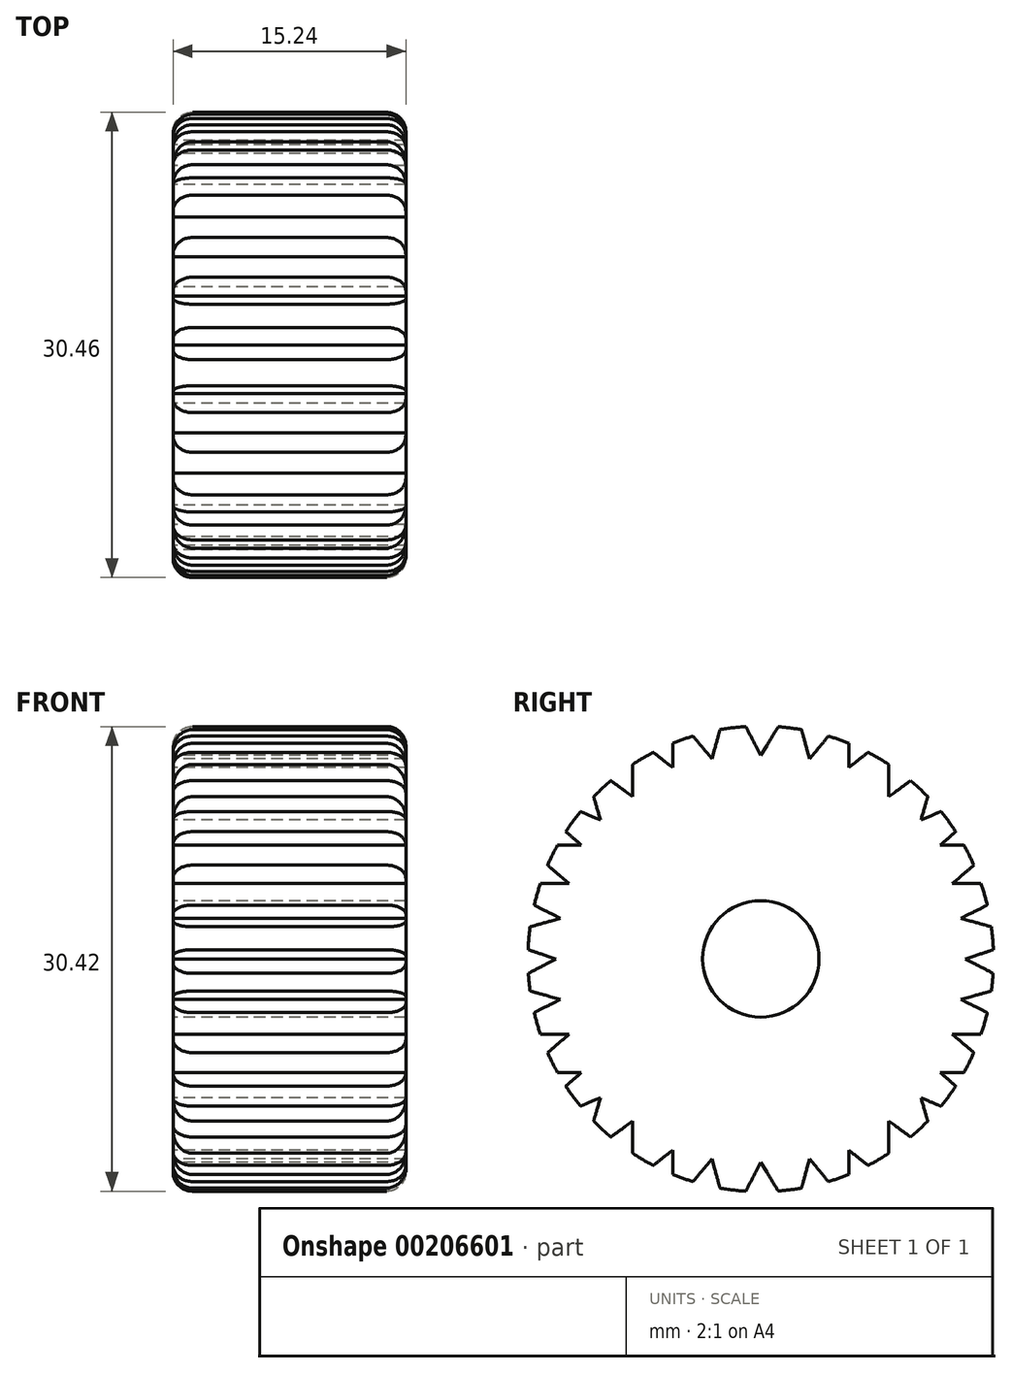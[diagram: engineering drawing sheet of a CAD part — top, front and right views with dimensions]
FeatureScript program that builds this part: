
annotation { "Feature Type Name" : "Feature", "Feature Type Description" : "" }
export const myFeature = defineFeature(function(context is Context, id is Id, definition is map)
    precondition{}
    {
        {
            var Q0;
            Q0=qCreatedBy(makeId("Right.planeOp"),FACE);
            var sketch = newSketch(context, id + "F0", { "sketchPlane" : qUnion([Q0])});
            skCircle(sketch, "E0", {"center": v(0, 0) * mm, "radius": 15.24 * mm});
            skLineSegment(sketch, "E1", {"start": v(11.8, 9.65) * mm, "end": v(10.5, 9.1) * mm});
            skLineSegment(sketch, "E2", {"start": v(10.5, 9.1) * mm, "end": v(10.94, 10.61) * mm});
            skLineSegment(sketch, "E3", {"start": v(12.76, 8.33) * mm, "end": v(11.74, 7.44) * mm});
            skLineSegment(sketch, "E4", {"start": v(11.74, 7.44) * mm, "end": v(13.3, 7.44) * mm});
            skLineSegment(sketch, "E5", {"start": v(14.83, 3.52) * mm, "end": v(13.11, 2.65) * mm});
            skLineSegment(sketch, "E6", {"start": v(13.11, 2.65) * mm, "end": v(15.1, 2.1) * mm});
            skLineSegment(sketch, "E7", {"start": v(13.95, 6.14) * mm, "end": v(12.54, 4.93) * mm});
            skLineSegment(sketch, "E8", {"start": v(12.54, 4.93) * mm, "end": v(14.42, 4.93) * mm});
            skLineSegment(sketch, "E9", {"start": v(15.23, 0.6) * mm, "end": v(13.4, 0) * mm});
            skLineSegment(sketch, "E10", {"start": v(13.4, 0) * mm, "end": v(15.21, -0.95) * mm});
            skLineSegment(sketch, "E11", {"start": v(9.8, 11.67) * mm, "end": v(8.38, 10.61) * mm});
            skLineSegment(sketch, "E12", {"start": v(8.38, 10.61) * mm, "end": v(8.38, 12.73) * mm});
            skLineSegment(sketch, "E13", {"start": v(7.03, 13.52) * mm, "end": v(5.76, 12.51) * mm});
            skLineSegment(sketch, "E14", {"start": v(5.76, 12.51) * mm, "end": v(5.76, 14.11) * mm});
            skLineSegment(sketch, "E15", {"start": v(4.43, 14.58) * mm, "end": v(3.2, 13.08) * mm});
            skLineSegment(sketch, "E16", {"start": v(3.2, 13.08) * mm, "end": v(2.67, 15) * mm});
            skLineSegment(sketch, "E17", {"start": v(1.15, 15.2) * mm, "end": v(0, 13.31) * mm});
            skPoint(sketch, "E17.endSnap0", {"position": v(5.76, 13.31) * mm});
            skLineSegment(sketch, "E18", {"start": v(0, 13.31) * mm, "end": v(-0.97, 15.2) * mm});
            skLineSegment(sketch, "E19.MirrorCS", {"start": v(-13.11, 2.65) * mm, "end": v(-15.1, 2.1) * mm});
            skLineSegment(sketch, "E20.MirrorCS", {"start": v(-14.83, 3.52) * mm, "end": v(-13.11, 2.65) * mm});
            skLineSegment(sketch, "E21.MirrorCS", {"start": v(-15.23, 0.6) * mm, "end": v(-13.4, 0) * mm});
            skLineSegment(sketch, "E22.MirrorCS", {"start": v(-13.4, 0) * mm, "end": v(-15.21, -0.95) * mm});
            skLineSegment(sketch, "E23.MirrorCS", {"start": v(-12.54, 4.93) * mm, "end": v(-14.42, 4.93) * mm});
            skLineSegment(sketch, "E24.MirrorCS", {"start": v(-13.95, 6.14) * mm, "end": v(-12.54, 4.93) * mm});
            skLineSegment(sketch, "E25.MirrorCS", {"start": v(-11.74, 7.44) * mm, "end": v(-13.3, 7.44) * mm});
            skLineSegment(sketch, "E26.MirrorCS", {"start": v(-12.76, 8.33) * mm, "end": v(-11.74, 7.44) * mm});
            skLineSegment(sketch, "E27.MirrorCS", {"start": v(-11.8, 9.65) * mm, "end": v(-10.5, 9.1) * mm});
            skLineSegment(sketch, "E28.MirrorCS", {"start": v(-10.5, 9.1) * mm, "end": v(-10.94, 10.61) * mm});
            skLineSegment(sketch, "E29.MirrorCS", {"start": v(-9.8, 11.67) * mm, "end": v(-8.38, 10.61) * mm});
            skLineSegment(sketch, "E30.MirrorCS", {"start": v(-8.38, 10.61) * mm, "end": v(-8.38, 12.73) * mm});
            skPoint(sketch, "E31.MirrorP", {"position": v(-5.76, 13.31) * mm});
            skLineSegment(sketch, "E32.MirrorCS", {"start": v(-7.03, 13.52) * mm, "end": v(-5.76, 12.51) * mm});
            skLineSegment(sketch, "E33.MirrorCS", {"start": v(-5.76, 12.51) * mm, "end": v(-5.76, 14.11) * mm});
            skLineSegment(sketch, "E34.MirrorCS", {"start": v(-4.43, 14.58) * mm, "end": v(-3.2, 13.08) * mm});
            skLineSegment(sketch, "E35.MirrorCS", {"start": v(-3.2, 13.08) * mm, "end": v(-2.67, 15) * mm});
            skLineSegment(sketch, "E36.MirrorCS", {"start": v(13.11, -2.65) * mm, "end": v(15.1, -2.1) * mm});
            skLineSegment(sketch, "E37.MirrorCS", {"start": v(14.83, -3.52) * mm, "end": v(13.11, -2.65) * mm});
            skLineSegment(sketch, "E38.MirrorCS", {"start": v(12.54, -4.93) * mm, "end": v(14.42, -4.93) * mm});
            skLineSegment(sketch, "E39.MirrorCS", {"start": v(13.95, -6.14) * mm, "end": v(12.54, -4.93) * mm});
            skLineSegment(sketch, "E40.MirrorCS", {"start": v(11.74, -7.44) * mm, "end": v(13.3, -7.44) * mm});
            skLineSegment(sketch, "E41.MirrorCS", {"start": v(12.76, -8.33) * mm, "end": v(11.74, -7.44) * mm});
            skLineSegment(sketch, "E42.MirrorCS", {"start": v(11.8, -9.65) * mm, "end": v(10.5, -9.1) * mm});
            skLineSegment(sketch, "E43.MirrorCS", {"start": v(10.5, -9.1) * mm, "end": v(10.94, -10.61) * mm});
            skLineSegment(sketch, "E44.MirrorCS", {"start": v(9.8, -11.67) * mm, "end": v(8.38, -10.61) * mm});
            skLineSegment(sketch, "E45.MirrorCS", {"start": v(8.38, -10.61) * mm, "end": v(8.38, -12.73) * mm});
            skLineSegment(sketch, "E46.MirrorCS", {"start": v(7.03, -13.52) * mm, "end": v(5.76, -12.51) * mm});
            skLineSegment(sketch, "E47.MirrorCS", {"start": v(5.76, -12.51) * mm, "end": v(5.76, -14.11) * mm});
            skLineSegment(sketch, "E48.MirrorCS", {"start": v(4.43, -14.58) * mm, "end": v(3.2, -13.08) * mm});
            skLineSegment(sketch, "E49.MirrorCS", {"start": v(3.2, -13.08) * mm, "end": v(2.67, -15) * mm});
            skLineSegment(sketch, "E50.MirrorCS", {"start": v(1.15, -15.2) * mm, "end": v(0, -13.31) * mm});
            skLineSegment(sketch, "E51.MirrorCS", {"start": v(0, -13.31) * mm, "end": v(-0.97, -15.2) * mm});
            skLineSegment(sketch, "E52.MirrorCS", {"start": v(-3.2, -13.08) * mm, "end": v(-2.67, -15) * mm});
            skLineSegment(sketch, "E53.MirrorCS", {"start": v(-4.43, -14.58) * mm, "end": v(-3.2, -13.08) * mm});
            skLineSegment(sketch, "E54.MirrorCS", {"start": v(-7.03, -13.52) * mm, "end": v(-5.76, -12.51) * mm});
            skLineSegment(sketch, "E55.MirrorCS", {"start": v(-5.76, -12.51) * mm, "end": v(-5.76, -14.11) * mm});
            skLineSegment(sketch, "E56.MirrorCS", {"start": v(-8.38, -10.61) * mm, "end": v(-8.38, -12.73) * mm});
            skLineSegment(sketch, "E57.MirrorCS", {"start": v(-9.8, -11.67) * mm, "end": v(-8.38, -10.61) * mm});
            skLineSegment(sketch, "E58.MirrorCS", {"start": v(-10.5, -9.1) * mm, "end": v(-10.94, -10.61) * mm});
            skLineSegment(sketch, "E59.MirrorCS", {"start": v(-11.8, -9.65) * mm, "end": v(-10.5, -9.1) * mm});
            skLineSegment(sketch, "E60.MirrorCS", {"start": v(-12.76, -8.33) * mm, "end": v(-11.74, -7.44) * mm});
            skLineSegment(sketch, "E61.MirrorCS", {"start": v(-11.74, -7.44) * mm, "end": v(-13.3, -7.44) * mm});
            skLineSegment(sketch, "E62.MirrorCS", {"start": v(-13.95, -6.14) * mm, "end": v(-12.54, -4.93) * mm});
            skLineSegment(sketch, "E63.MirrorCS", {"start": v(-12.54, -4.93) * mm, "end": v(-14.42, -4.93) * mm});
            skLineSegment(sketch, "E64.MirrorCS", {"start": v(-14.83, -3.52) * mm, "end": v(-13.11, -2.65) * mm});
            skLineSegment(sketch, "E65.MirrorCS", {"start": v(-13.11, -2.65) * mm, "end": v(-15.1, -2.1) * mm});
            skSolve(sketch);
        }
        {
            var Q0;
            {var subQ14=sQuery(id+"F0.wireOp",EDGE,"E1");Q0=makeQuery(id+"F0.imprint","IMPRINT",FACE,{"disambiguationData":[TD([[makeQuery(id+"F0.imprint","IMPRINT",EDGE,{"derivedFrom":subQ14}),1.0]])]});}
            extrude(context, id + "F1", {"entities" : qUnion([Q0]), "depth" : 15.24 * mm});
        }
        {
            var Q0;
            Q0=makeQuery(id+"F1.opExtrude","CAP_FACE",FACE,{"disambiguationData":[OSD([sQuery(id+"F0.wireOp",EDGE,"E0"),sQuery(id+"F0.wireOp",EDGE,"E1"),sQuery(id+"F0.wireOp",EDGE,"E2"),sQuery(id+"F0.wireOp",EDGE,"E3"),sQuery(id+"F0.wireOp",EDGE,"E4"),sQuery(id+"F0.wireOp",EDGE,"E5"),sQuery(id+"F0.wireOp",EDGE,"E6"),sQuery(id+"F0.wireOp",EDGE,"E7"),sQuery(id+"F0.wireOp",EDGE,"E8"),sQuery(id+"F0.wireOp",EDGE,"E9"),sQuery(id+"F0.wireOp",EDGE,"E10"),sQuery(id+"F0.wireOp",EDGE,"E11"),sQuery(id+"F0.wireOp",EDGE,"E12"),sQuery(id+"F0.wireOp",EDGE,"E13"),sQuery(id+"F0.wireOp",EDGE,"E14"),sQuery(id+"F0.wireOp",EDGE,"E15"),sQuery(id+"F0.wireOp",EDGE,"E16"),sQuery(id+"F0.wireOp",EDGE,"E17"),sQuery(id+"F0.wireOp",EDGE,"E18"),sQuery(id+"F0.wireOp",EDGE,"E19.MirrorCS"),sQuery(id+"F0.wireOp",EDGE,"E20.MirrorCS"),sQuery(id+"F0.wireOp",EDGE,"E21.MirrorCS"),sQuery(id+"F0.wireOp",EDGE,"E22.MirrorCS"),sQuery(id+"F0.wireOp",EDGE,"E23.MirrorCS"),sQuery(id+"F0.wireOp",EDGE,"E24.MirrorCS"),sQuery(id+"F0.wireOp",EDGE,"E25.MirrorCS"),sQuery(id+"F0.wireOp",EDGE,"E26.MirrorCS"),sQuery(id+"F0.wireOp",EDGE,"E27.MirrorCS"),sQuery(id+"F0.wireOp",EDGE,"E28.MirrorCS"),sQuery(id+"F0.wireOp",EDGE,"E29.MirrorCS"),sQuery(id+"F0.wireOp",EDGE,"E30.MirrorCS"),sQuery(id+"F0.wireOp",EDGE,"E32.MirrorCS"),sQuery(id+"F0.wireOp",EDGE,"E33.MirrorCS"),sQuery(id+"F0.wireOp",EDGE,"E34.MirrorCS"),sQuery(id+"F0.wireOp",EDGE,"E35.MirrorCS"),sQuery(id+"F0.wireOp",EDGE,"E36.MirrorCS"),sQuery(id+"F0.wireOp",EDGE,"E37.MirrorCS"),sQuery(id+"F0.wireOp",EDGE,"E38.MirrorCS"),sQuery(id+"F0.wireOp",EDGE,"E39.MirrorCS"),sQuery(id+"F0.wireOp",EDGE,"E40.MirrorCS"),sQuery(id+"F0.wireOp",EDGE,"E41.MirrorCS"),sQuery(id+"F0.wireOp",EDGE,"E42.MirrorCS"),sQuery(id+"F0.wireOp",EDGE,"E43.MirrorCS"),sQuery(id+"F0.wireOp",EDGE,"E44.MirrorCS"),sQuery(id+"F0.wireOp",EDGE,"E45.MirrorCS"),sQuery(id+"F0.wireOp",EDGE,"E46.MirrorCS"),sQuery(id+"F0.wireOp",EDGE,"E47.MirrorCS"),sQuery(id+"F0.wireOp",EDGE,"E48.MirrorCS"),sQuery(id+"F0.wireOp",EDGE,"E49.MirrorCS"),sQuery(id+"F0.wireOp",EDGE,"E50.MirrorCS"),sQuery(id+"F0.wireOp",EDGE,"E51.MirrorCS"),sQuery(id+"F0.wireOp",EDGE,"E52.MirrorCS"),sQuery(id+"F0.wireOp",EDGE,"E53.MirrorCS"),sQuery(id+"F0.wireOp",EDGE,"E54.MirrorCS"),sQuery(id+"F0.wireOp",EDGE,"E55.MirrorCS"),sQuery(id+"F0.wireOp",EDGE,"E56.MirrorCS"),sQuery(id+"F0.wireOp",EDGE,"E57.MirrorCS"),sQuery(id+"F0.wireOp",EDGE,"E58.MirrorCS"),sQuery(id+"F0.wireOp",EDGE,"E59.MirrorCS"),sQuery(id+"F0.wireOp",EDGE,"E60.MirrorCS"),sQuery(id+"F0.wireOp",EDGE,"E61.MirrorCS"),sQuery(id+"F0.wireOp",EDGE,"E62.MirrorCS"),sQuery(id+"F0.wireOp",EDGE,"E63.MirrorCS"),sQuery(id+"F0.wireOp",EDGE,"E64.MirrorCS"),sQuery(id+"F0.wireOp",EDGE,"E65.MirrorCS")])],"isStart":true});
            var sketch = newSketch(context, id + "F2", { "sketchPlane" : qUnion([Q0])});
            skCircle(sketch, "E66", {"center": v(0, 0) * mm, "radius": 3.81 * mm});
            skSolve(sketch);
        }
        {
            var Q0;
            Q0=makeQuery(id+"F2.imprint","IMPRINT",FACE,{"disambiguationData":[TD([[makeQuery(id+"F2.imprint","IMPRINT",EDGE,{"derivedFrom":sQuery(id+"F2.wireOp",EDGE,"E66")}),1.0]])]});
            var Q1;
            Q1=sQuery(id+"F2.wireOp",EDGE,"E66");
            extrude(context, id + "F3", {"entities" : qUnion([Q0]), "operationType" : NewBodyOperationType.REMOVE, "surfaceEntities" : qUnion([Q1]), "oppositeDirection" : true, "depth" : 38.1 * mm});
        }
        {
            var Q0;
            {var subQ0=sQuery(id+"F0.wireOp",EDGE,"E0");Q0=makeQuery(id+"F1.opExtrude","CAP_EDGE",EDGE,{"disambiguationData":[OSD([subQ0]),TDD([makeQuery(id+"F0.imprint","IMPRINT",EDGE,{"disambiguationData":[TD([[makeQuery(id+"F0.imprint","INTERSECT",VERTEX,{"derivedFrom":[subQ0,sQuery(id+"F0.wireOp",EDGE,"E51.MirrorCS")]}),1.0]])],"derivedFrom":subQ0})])],"isStart":true});}
            var Q1;
            {var subQ0=sQuery(id+"F0.wireOp",EDGE,"E0");Q1=makeQuery(id+"F1.opExtrude","CAP_EDGE",EDGE,{"disambiguationData":[OSD([subQ0]),TDD([makeQuery(id+"F0.imprint","IMPRINT",EDGE,{"disambiguationData":[TD([[makeQuery(id+"F0.imprint","INTERSECT",VERTEX,{"derivedFrom":[subQ0,sQuery(id+"F0.wireOp",EDGE,"E49.MirrorCS")]}),1.0]])],"derivedFrom":subQ0})])],"isStart":true});}
            var Q2;
            {var subQ0=sQuery(id+"F0.wireOp",EDGE,"E0");Q2=makeQuery(id+"F1.opExtrude","CAP_EDGE",EDGE,{"disambiguationData":[OSD([subQ0]),TDD([makeQuery(id+"F0.imprint","IMPRINT",EDGE,{"disambiguationData":[TD([[makeQuery(id+"F0.imprint","INTERSECT",VERTEX,{"derivedFrom":[subQ0,sQuery(id+"F0.wireOp",EDGE,"E47.MirrorCS")]}),1.0]])],"derivedFrom":subQ0})])],"isStart":true});}
            var Q3;
            {var subQ0=sQuery(id+"F0.wireOp",EDGE,"E0");Q3=makeQuery(id+"F1.opExtrude","CAP_EDGE",EDGE,{"disambiguationData":[OSD([subQ0]),TDD([makeQuery(id+"F0.imprint","IMPRINT",EDGE,{"disambiguationData":[TD([[makeQuery(id+"F0.imprint","INTERSECT",VERTEX,{"derivedFrom":[subQ0,sQuery(id+"F0.wireOp",EDGE,"E61.MirrorCS")]}),1.0]])],"derivedFrom":subQ0})])],"isStart":true});}
            var Q4;
            {var subQ0=sQuery(id+"F0.wireOp",EDGE,"E0");Q4=makeQuery(id+"F1.opExtrude","CAP_EDGE",EDGE,{"disambiguationData":[OSD([subQ0]),TDD([makeQuery(id+"F0.imprint","IMPRINT",EDGE,{"disambiguationData":[TD([[makeQuery(id+"F0.imprint","INTERSECT",VERTEX,{"derivedFrom":[subQ0,sQuery(id+"F0.wireOp",EDGE,"E59.MirrorCS")]}),1.0]])],"derivedFrom":subQ0})])],"isStart":true});}
            var Q5;
            {var subQ0=sQuery(id+"F0.wireOp",EDGE,"E0");Q5=makeQuery(id+"F1.opExtrude","CAP_EDGE",EDGE,{"disambiguationData":[OSD([subQ0]),TDD([makeQuery(id+"F0.imprint","IMPRINT",EDGE,{"disambiguationData":[TD([[makeQuery(id+"F0.imprint","INTERSECT",VERTEX,{"derivedFrom":[subQ0,sQuery(id+"F0.wireOp",EDGE,"E57.MirrorCS")]}),1.0]])],"derivedFrom":subQ0})])],"isStart":true});}
            var Q6;
            {var subQ0=sQuery(id+"F0.wireOp",EDGE,"E0");Q6=makeQuery(id+"F1.opExtrude","CAP_EDGE",EDGE,{"disambiguationData":[OSD([subQ0]),TDD([makeQuery(id+"F0.imprint","IMPRINT",EDGE,{"disambiguationData":[TD([[makeQuery(id+"F0.imprint","INTERSECT",VERTEX,{"derivedFrom":[subQ0,sQuery(id+"F0.wireOp",EDGE,"E54.MirrorCS")]}),1.0]])],"derivedFrom":subQ0})])],"isStart":true});}
            var Q7;
            {var subQ0=sQuery(id+"F0.wireOp",EDGE,"E0");Q7=makeQuery(id+"F1.opExtrude","CAP_EDGE",EDGE,{"disambiguationData":[OSD([subQ0]),TDD([makeQuery(id+"F0.imprint","IMPRINT",EDGE,{"disambiguationData":[TD([[makeQuery(id+"F0.imprint","INTERSECT",VERTEX,{"derivedFrom":[subQ0,sQuery(id+"F0.wireOp",EDGE,"E63.MirrorCS")]}),1.0]])],"derivedFrom":subQ0})])],"isStart":true});}
            var Q8;
            {var subQ0=sQuery(id+"F0.wireOp",EDGE,"E0");Q8=makeQuery(id+"F1.opExtrude","CAP_EDGE",EDGE,{"disambiguationData":[OSD([subQ0]),TDD([makeQuery(id+"F0.imprint","IMPRINT",EDGE,{"disambiguationData":[TD([[makeQuery(id+"F0.imprint","INTERSECT",VERTEX,{"derivedFrom":[subQ0,sQuery(id+"F0.wireOp",EDGE,"E19.MirrorCS")]}),-1.0]])],"derivedFrom":subQ0})])],"isStart":true});}
            var Q9;
            {var subQ0=sQuery(id+"F0.wireOp",EDGE,"E0");Q9=makeQuery(id+"F1.opExtrude","CAP_EDGE",EDGE,{"disambiguationData":[OSD([subQ0]),TDD([makeQuery(id+"F0.imprint","IMPRINT",EDGE,{"disambiguationData":[TD([[makeQuery(id+"F0.imprint","INTERSECT",VERTEX,{"derivedFrom":[subQ0,sQuery(id+"F0.wireOp",EDGE,"E22.MirrorCS")]}),-1.0]])],"derivedFrom":subQ0})])],"isStart":true});}
            var Q10;
            {var subQ0=sQuery(id+"F0.wireOp",EDGE,"E0");Q10=makeQuery(id+"F1.opExtrude","CAP_EDGE",EDGE,{"disambiguationData":[OSD([subQ0]),TDD([makeQuery(id+"F0.imprint","IMPRINT",EDGE,{"disambiguationData":[TD([[makeQuery(id+"F0.imprint","INTERSECT",VERTEX,{"derivedFrom":[subQ0,sQuery(id+"F0.wireOp",EDGE,"E20.MirrorCS")]}),1.0]])],"derivedFrom":subQ0})])],"isStart":true});}
            var Q11;
            {var subQ0=sQuery(id+"F0.wireOp",EDGE,"E0");Q11=makeQuery(id+"F1.opExtrude","CAP_EDGE",EDGE,{"disambiguationData":[OSD([subQ0]),TDD([makeQuery(id+"F0.imprint","IMPRINT",EDGE,{"disambiguationData":[TD([[makeQuery(id+"F0.imprint","INTERSECT",VERTEX,{"derivedFrom":[subQ0,sQuery(id+"F0.wireOp",EDGE,"E24.MirrorCS")]}),1.0]])],"derivedFrom":subQ0})])],"isStart":true});}
            var Q12;
            {var subQ0=sQuery(id+"F0.wireOp",EDGE,"E0");Q12=makeQuery(id+"F1.opExtrude","CAP_EDGE",EDGE,{"disambiguationData":[OSD([subQ0]),TDD([makeQuery(id+"F0.imprint","IMPRINT",EDGE,{"disambiguationData":[TD([[makeQuery(id+"F0.imprint","INTERSECT",VERTEX,{"derivedFrom":[subQ0,sQuery(id+"F0.wireOp",EDGE,"E26.MirrorCS")]}),1.0]])],"derivedFrom":subQ0})])],"isStart":true});}
            var Q13;
            {var subQ0=sQuery(id+"F0.wireOp",EDGE,"E0");Q13=makeQuery(id+"F1.opExtrude","CAP_EDGE",EDGE,{"disambiguationData":[OSD([subQ0]),TDD([makeQuery(id+"F0.imprint","IMPRINT",EDGE,{"disambiguationData":[TD([[makeQuery(id+"F0.imprint","INTERSECT",VERTEX,{"derivedFrom":[subQ0,sQuery(id+"F0.wireOp",EDGE,"E53.MirrorCS")]}),1.0]])],"derivedFrom":subQ0})])],"isStart":true});}
            var Q14;
            {var subQ0=sQuery(id+"F0.wireOp",EDGE,"E0");Q14=makeQuery(id+"F1.opExtrude","CAP_EDGE",EDGE,{"disambiguationData":[OSD([subQ0]),TDD([makeQuery(id+"F0.imprint","IMPRINT",EDGE,{"disambiguationData":[TD([[makeQuery(id+"F0.imprint","INTERSECT",VERTEX,{"derivedFrom":[subQ0,sQuery(id+"F0.wireOp",EDGE,"E45.MirrorCS")]}),1.0]])],"derivedFrom":subQ0})])],"isStart":true});}
            var Q15;
            {var subQ0=sQuery(id+"F0.wireOp",EDGE,"E0");Q15=makeQuery(id+"F1.opExtrude","CAP_EDGE",EDGE,{"disambiguationData":[OSD([subQ0]),TDD([makeQuery(id+"F0.imprint","IMPRINT",EDGE,{"disambiguationData":[TD([[makeQuery(id+"F0.imprint","INTERSECT",VERTEX,{"derivedFrom":[subQ0,sQuery(id+"F0.wireOp",EDGE,"E43.MirrorCS")]}),1.0]])],"derivedFrom":subQ0})])],"isStart":true});}
            var Q16;
            {var subQ0=sQuery(id+"F0.wireOp",EDGE,"E0");Q16=makeQuery(id+"F1.opExtrude","CAP_EDGE",EDGE,{"disambiguationData":[OSD([subQ0]),TDD([makeQuery(id+"F0.imprint","IMPRINT",EDGE,{"disambiguationData":[TD([[makeQuery(id+"F0.imprint","INTERSECT",VERTEX,{"derivedFrom":[subQ0,sQuery(id+"F0.wireOp",EDGE,"E41.MirrorCS")]}),1.0]])],"derivedFrom":subQ0})])],"isStart":true});}
            var Q17;
            {var subQ0=sQuery(id+"F0.wireOp",EDGE,"E0");Q17=makeQuery(id+"F1.opExtrude","CAP_EDGE",EDGE,{"disambiguationData":[OSD([subQ0]),TDD([makeQuery(id+"F0.imprint","IMPRINT",EDGE,{"disambiguationData":[TD([[makeQuery(id+"F0.imprint","INTERSECT",VERTEX,{"derivedFrom":[subQ0,sQuery(id+"F0.wireOp",EDGE,"E39.MirrorCS")]}),1.0]])],"derivedFrom":subQ0})])],"isStart":true});}
            var Q18;
            {var subQ0=sQuery(id+"F0.wireOp",EDGE,"E0");Q18=makeQuery(id+"F1.opExtrude","CAP_EDGE",EDGE,{"disambiguationData":[OSD([subQ0]),TDD([makeQuery(id+"F0.imprint","IMPRINT",EDGE,{"disambiguationData":[TD([[makeQuery(id+"F0.imprint","INTERSECT",VERTEX,{"derivedFrom":[subQ0,sQuery(id+"F0.wireOp",EDGE,"E28.MirrorCS")]}),1.0]])],"derivedFrom":subQ0})])],"isStart":true});}
            var Q19;
            {var subQ0=sQuery(id+"F0.wireOp",EDGE,"E0");Q19=makeQuery(id+"F1.opExtrude","CAP_EDGE",EDGE,{"disambiguationData":[OSD([subQ0]),TDD([makeQuery(id+"F0.imprint","IMPRINT",EDGE,{"disambiguationData":[TD([[makeQuery(id+"F0.imprint","INTERSECT",VERTEX,{"derivedFrom":[subQ0,sQuery(id+"F0.wireOp",EDGE,"E30.MirrorCS")]}),1.0]])],"derivedFrom":subQ0})])],"isStart":true});}
            var Q20;
            {var subQ0=sQuery(id+"F0.wireOp",EDGE,"E0");Q20=makeQuery(id+"F1.opExtrude","CAP_EDGE",EDGE,{"disambiguationData":[OSD([subQ0]),TDD([makeQuery(id+"F0.imprint","IMPRINT",EDGE,{"disambiguationData":[TD([[makeQuery(id+"F0.imprint","INTERSECT",VERTEX,{"derivedFrom":[subQ0,sQuery(id+"F0.wireOp",EDGE,"E33.MirrorCS")]}),1.0]])],"derivedFrom":subQ0})])],"isStart":true});}
            var Q21;
            {var subQ0=sQuery(id+"F0.wireOp",EDGE,"E0");Q21=makeQuery(id+"F1.opExtrude","CAP_EDGE",EDGE,{"disambiguationData":[OSD([subQ0]),TDD([makeQuery(id+"F0.imprint","IMPRINT",EDGE,{"disambiguationData":[TD([[makeQuery(id+"F0.imprint","INTERSECT",VERTEX,{"derivedFrom":[subQ0,sQuery(id+"F0.wireOp",EDGE,"E18")]}),-1.0]])],"derivedFrom":subQ0})])],"isStart":true});}
            var Q22;
            {var subQ0=sQuery(id+"F0.wireOp",EDGE,"E0");Q22=makeQuery(id+"F1.opExtrude","CAP_EDGE",EDGE,{"disambiguationData":[OSD([subQ0]),TDD([makeQuery(id+"F0.imprint","IMPRINT",EDGE,{"disambiguationData":[TD([[makeQuery(id+"F0.imprint","INTERSECT",VERTEX,{"derivedFrom":[subQ0,sQuery(id+"F0.wireOp",EDGE,"E16")]}),-1.0]])],"derivedFrom":subQ0})])],"isStart":true});}
            var Q23;
            {var subQ0=sQuery(id+"F0.wireOp",EDGE,"E0");Q23=makeQuery(id+"F1.opExtrude","CAP_EDGE",EDGE,{"disambiguationData":[OSD([subQ0]),TDD([makeQuery(id+"F0.imprint","IMPRINT",EDGE,{"disambiguationData":[TD([[makeQuery(id+"F0.imprint","INTERSECT",VERTEX,{"derivedFrom":[subQ0,sQuery(id+"F0.wireOp",EDGE,"E14")]}),-1.0]])],"derivedFrom":subQ0})])],"isStart":true});}
            var Q24;
            {var subQ0=sQuery(id+"F0.wireOp",EDGE,"E0");Q24=makeQuery(id+"F1.opExtrude","CAP_EDGE",EDGE,{"disambiguationData":[OSD([subQ0]),TDD([makeQuery(id+"F0.imprint","IMPRINT",EDGE,{"disambiguationData":[TD([[makeQuery(id+"F0.imprint","INTERSECT",VERTEX,{"derivedFrom":[subQ0,sQuery(id+"F0.wireOp",EDGE,"E12")]}),-1.0]])],"derivedFrom":subQ0})])],"isStart":true});}
            var Q25;
            {var subQ0=sQuery(id+"F0.wireOp",EDGE,"E0");Q25=makeQuery(id+"F1.opExtrude","CAP_EDGE",EDGE,{"disambiguationData":[OSD([subQ0]),TDD([makeQuery(id+"F0.imprint","IMPRINT",EDGE,{"disambiguationData":[TD([[makeQuery(id+"F0.imprint","INTERSECT",VERTEX,{"derivedFrom":[subQ0,sQuery(id+"F0.wireOp",EDGE,"E2")]}),-1.0]])],"derivedFrom":subQ0})])],"isStart":true});}
            var Q26;
            {var subQ0=sQuery(id+"F0.wireOp",EDGE,"E0");Q26=makeQuery(id+"F1.opExtrude","CAP_EDGE",EDGE,{"disambiguationData":[OSD([subQ0]),TDD([makeQuery(id+"F0.imprint","IMPRINT",EDGE,{"disambiguationData":[TD([[makeQuery(id+"F0.imprint","INTERSECT",VERTEX,{"derivedFrom":[subQ0,sQuery(id+"F0.wireOp",EDGE,"E1")]}),1.0]])],"derivedFrom":subQ0})])],"isStart":true});}
            var Q27;
            {var subQ0=sQuery(id+"F0.wireOp",EDGE,"E0");Q27=makeQuery(id+"F1.opExtrude","CAP_EDGE",EDGE,{"disambiguationData":[OSD([subQ0]),TDD([makeQuery(id+"F0.imprint","IMPRINT",EDGE,{"disambiguationData":[TD([[makeQuery(id+"F0.imprint","INTERSECT",VERTEX,{"derivedFrom":[subQ0,sQuery(id+"F0.wireOp",EDGE,"E4")]}),1.0]])],"derivedFrom":subQ0})])],"isStart":true});}
            var Q28;
            {var subQ0=sQuery(id+"F0.wireOp",EDGE,"E0");Q28=makeQuery(id+"F1.opExtrude","CAP_EDGE",EDGE,{"disambiguationData":[OSD([subQ0]),TDD([makeQuery(id+"F0.imprint","IMPRINT",EDGE,{"disambiguationData":[TD([[makeQuery(id+"F0.imprint","INTERSECT",VERTEX,{"derivedFrom":[subQ0,sQuery(id+"F0.wireOp",EDGE,"E5")]}),-1.0]])],"derivedFrom":subQ0})])],"isStart":true});}
            var Q29;
            {var subQ0=sQuery(id+"F0.wireOp",EDGE,"E0");Q29=makeQuery(id+"F1.opExtrude","CAP_EDGE",EDGE,{"disambiguationData":[OSD([subQ0]),TDD([makeQuery(id+"F0.imprint","IMPRINT",EDGE,{"disambiguationData":[TD([[makeQuery(id+"F0.imprint","INTERSECT",VERTEX,{"derivedFrom":[subQ0,sQuery(id+"F0.wireOp",EDGE,"E37.MirrorCS")]}),1.0]])],"derivedFrom":subQ0})])],"isStart":true});}
            var Q30;
            {var subQ0=sQuery(id+"F0.wireOp",EDGE,"E0");Q30=makeQuery(id+"F1.opExtrude","CAP_EDGE",EDGE,{"disambiguationData":[OSD([subQ0]),TDD([makeQuery(id+"F0.imprint","IMPRINT",EDGE,{"disambiguationData":[TD([[makeQuery(id+"F0.imprint","INTERSECT",VERTEX,{"derivedFrom":[subQ0,sQuery(id+"F0.wireOp",EDGE,"E10")]}),1.0]])],"derivedFrom":subQ0})])],"isStart":true});}
            var Q31;
            {var subQ0=sQuery(id+"F0.wireOp",EDGE,"E0");Q31=makeQuery(id+"F1.opExtrude","CAP_EDGE",EDGE,{"disambiguationData":[OSD([subQ0]),TDD([makeQuery(id+"F0.imprint","IMPRINT",EDGE,{"disambiguationData":[TD([[makeQuery(id+"F0.imprint","INTERSECT",VERTEX,{"derivedFrom":[subQ0,sQuery(id+"F0.wireOp",EDGE,"E6")]}),1.0]])],"derivedFrom":subQ0})])],"isStart":true});}
            fillet(context, id + "F4", {"entities" : qUnion([Q0, Q1, Q2, Q3, Q4, Q5, Q6, Q7, Q8, Q9, Q10, Q11, Q12, Q13, Q14, Q15, Q16, Q17, Q18, Q19, Q20, Q21, Q22, Q23, Q24, Q25, Q26, Q27, Q28, Q29, Q30, Q31]), "radius" : 1.27 * mm, "tangentPropagation" : true, "allowEdgeOverflow" : false});
        }
        {
            var Q0;
            {var subQ0=sQuery(id+"F0.wireOp",EDGE,"E0");Q0=makeQuery(id+"F1.opExtrude","CAP_EDGE",EDGE,{"disambiguationData":[OSD([subQ0]),TDD([makeQuery(id+"F0.imprint","IMPRINT",EDGE,{"disambiguationData":[TD([[makeQuery(id+"F0.imprint","INTERSECT",VERTEX,{"derivedFrom":[subQ0,sQuery(id+"F0.wireOp",EDGE,"E37.MirrorCS")]}),1.0]])],"derivedFrom":subQ0})])],"isStart":false});}
            var Q1;
            {var subQ0=sQuery(id+"F0.wireOp",EDGE,"E0");Q1=makeQuery(id+"F1.opExtrude","CAP_EDGE",EDGE,{"disambiguationData":[OSD([subQ0]),TDD([makeQuery(id+"F0.imprint","IMPRINT",EDGE,{"disambiguationData":[TD([[makeQuery(id+"F0.imprint","INTERSECT",VERTEX,{"derivedFrom":[subQ0,sQuery(id+"F0.wireOp",EDGE,"E39.MirrorCS")]}),1.0]])],"derivedFrom":subQ0})])],"isStart":false});}
            var Q2;
            {var subQ0=sQuery(id+"F0.wireOp",EDGE,"E0");Q2=makeQuery(id+"F1.opExtrude","CAP_EDGE",EDGE,{"disambiguationData":[OSD([subQ0]),TDD([makeQuery(id+"F0.imprint","IMPRINT",EDGE,{"disambiguationData":[TD([[makeQuery(id+"F0.imprint","INTERSECT",VERTEX,{"derivedFrom":[subQ0,sQuery(id+"F0.wireOp",EDGE,"E41.MirrorCS")]}),1.0]])],"derivedFrom":subQ0})])],"isStart":false});}
            var Q3;
            {var subQ0=sQuery(id+"F0.wireOp",EDGE,"E0");Q3=makeQuery(id+"F1.opExtrude","CAP_EDGE",EDGE,{"disambiguationData":[OSD([subQ0]),TDD([makeQuery(id+"F0.imprint","IMPRINT",EDGE,{"disambiguationData":[TD([[makeQuery(id+"F0.imprint","INTERSECT",VERTEX,{"derivedFrom":[subQ0,sQuery(id+"F0.wireOp",EDGE,"E43.MirrorCS")]}),1.0]])],"derivedFrom":subQ0})])],"isStart":false});}
            var Q4;
            {var subQ0=sQuery(id+"F0.wireOp",EDGE,"E0");Q4=makeQuery(id+"F1.opExtrude","CAP_EDGE",EDGE,{"disambiguationData":[OSD([subQ0]),TDD([makeQuery(id+"F0.imprint","IMPRINT",EDGE,{"disambiguationData":[TD([[makeQuery(id+"F0.imprint","INTERSECT",VERTEX,{"derivedFrom":[subQ0,sQuery(id+"F0.wireOp",EDGE,"E10")]}),1.0]])],"derivedFrom":subQ0})])],"isStart":false});}
            var Q5;
            {var subQ0=sQuery(id+"F0.wireOp",EDGE,"E0");Q5=makeQuery(id+"F1.opExtrude","CAP_EDGE",EDGE,{"disambiguationData":[OSD([subQ0]),TDD([makeQuery(id+"F0.imprint","IMPRINT",EDGE,{"disambiguationData":[TD([[makeQuery(id+"F0.imprint","INTERSECT",VERTEX,{"derivedFrom":[subQ0,sQuery(id+"F0.wireOp",EDGE,"E6")]}),1.0]])],"derivedFrom":subQ0})])],"isStart":false});}
            var Q6;
            {var subQ0=sQuery(id+"F0.wireOp",EDGE,"E0");Q6=makeQuery(id+"F1.opExtrude","CAP_EDGE",EDGE,{"disambiguationData":[OSD([subQ0]),TDD([makeQuery(id+"F0.imprint","IMPRINT",EDGE,{"disambiguationData":[TD([[makeQuery(id+"F0.imprint","INTERSECT",VERTEX,{"derivedFrom":[subQ0,sQuery(id+"F0.wireOp",EDGE,"E5")]}),-1.0]])],"derivedFrom":subQ0})])],"isStart":false});}
            var Q7;
            {var subQ0=sQuery(id+"F0.wireOp",EDGE,"E0");Q7=makeQuery(id+"F1.opExtrude","CAP_EDGE",EDGE,{"disambiguationData":[OSD([subQ0]),TDD([makeQuery(id+"F0.imprint","IMPRINT",EDGE,{"disambiguationData":[TD([[makeQuery(id+"F0.imprint","INTERSECT",VERTEX,{"derivedFrom":[subQ0,sQuery(id+"F0.wireOp",EDGE,"E4")]}),1.0]])],"derivedFrom":subQ0})])],"isStart":false});}
            var Q8;
            {var subQ0=sQuery(id+"F0.wireOp",EDGE,"E0");Q8=makeQuery(id+"F1.opExtrude","CAP_EDGE",EDGE,{"disambiguationData":[OSD([subQ0]),TDD([makeQuery(id+"F0.imprint","IMPRINT",EDGE,{"disambiguationData":[TD([[makeQuery(id+"F0.imprint","INTERSECT",VERTEX,{"derivedFrom":[subQ0,sQuery(id+"F0.wireOp",EDGE,"E1")]}),1.0]])],"derivedFrom":subQ0})])],"isStart":false});}
            var Q9;
            {var subQ0=sQuery(id+"F0.wireOp",EDGE,"E0");Q9=makeQuery(id+"F1.opExtrude","CAP_EDGE",EDGE,{"disambiguationData":[OSD([subQ0]),TDD([makeQuery(id+"F0.imprint","IMPRINT",EDGE,{"disambiguationData":[TD([[makeQuery(id+"F0.imprint","INTERSECT",VERTEX,{"derivedFrom":[subQ0,sQuery(id+"F0.wireOp",EDGE,"E2")]}),-1.0]])],"derivedFrom":subQ0})])],"isStart":false});}
            var Q10;
            {var subQ0=sQuery(id+"F0.wireOp",EDGE,"E0");Q10=makeQuery(id+"F1.opExtrude","CAP_EDGE",EDGE,{"disambiguationData":[OSD([subQ0]),TDD([makeQuery(id+"F0.imprint","IMPRINT",EDGE,{"disambiguationData":[TD([[makeQuery(id+"F0.imprint","INTERSECT",VERTEX,{"derivedFrom":[subQ0,sQuery(id+"F0.wireOp",EDGE,"E12")]}),-1.0]])],"derivedFrom":subQ0})])],"isStart":false});}
            var Q11;
            {var subQ0=sQuery(id+"F0.wireOp",EDGE,"E0");Q11=makeQuery(id+"F1.opExtrude","CAP_EDGE",EDGE,{"disambiguationData":[OSD([subQ0]),TDD([makeQuery(id+"F0.imprint","IMPRINT",EDGE,{"disambiguationData":[TD([[makeQuery(id+"F0.imprint","INTERSECT",VERTEX,{"derivedFrom":[subQ0,sQuery(id+"F0.wireOp",EDGE,"E14")]}),-1.0]])],"derivedFrom":subQ0})])],"isStart":false});}
            var Q12;
            {var subQ0=sQuery(id+"F0.wireOp",EDGE,"E0");Q12=makeQuery(id+"F1.opExtrude","CAP_EDGE",EDGE,{"disambiguationData":[OSD([subQ0]),TDD([makeQuery(id+"F0.imprint","IMPRINT",EDGE,{"disambiguationData":[TD([[makeQuery(id+"F0.imprint","INTERSECT",VERTEX,{"derivedFrom":[subQ0,sQuery(id+"F0.wireOp",EDGE,"E16")]}),-1.0]])],"derivedFrom":subQ0})])],"isStart":false});}
            var Q13;
            {var subQ0=sQuery(id+"F0.wireOp",EDGE,"E0");Q13=makeQuery(id+"F1.opExtrude","CAP_EDGE",EDGE,{"disambiguationData":[OSD([subQ0]),TDD([makeQuery(id+"F0.imprint","IMPRINT",EDGE,{"disambiguationData":[TD([[makeQuery(id+"F0.imprint","INTERSECT",VERTEX,{"derivedFrom":[subQ0,sQuery(id+"F0.wireOp",EDGE,"E18")]}),-1.0]])],"derivedFrom":subQ0})])],"isStart":false});}
            var Q14;
            {var subQ0=sQuery(id+"F0.wireOp",EDGE,"E0");Q14=makeQuery(id+"F1.opExtrude","CAP_EDGE",EDGE,{"disambiguationData":[OSD([subQ0]),TDD([makeQuery(id+"F0.imprint","IMPRINT",EDGE,{"disambiguationData":[TD([[makeQuery(id+"F0.imprint","INTERSECT",VERTEX,{"derivedFrom":[subQ0,sQuery(id+"F0.wireOp",EDGE,"E33.MirrorCS")]}),1.0]])],"derivedFrom":subQ0})])],"isStart":false});}
            var Q15;
            {var subQ0=sQuery(id+"F0.wireOp",EDGE,"E0");Q15=makeQuery(id+"F1.opExtrude","CAP_EDGE",EDGE,{"disambiguationData":[OSD([subQ0]),TDD([makeQuery(id+"F0.imprint","IMPRINT",EDGE,{"disambiguationData":[TD([[makeQuery(id+"F0.imprint","INTERSECT",VERTEX,{"derivedFrom":[subQ0,sQuery(id+"F0.wireOp",EDGE,"E30.MirrorCS")]}),1.0]])],"derivedFrom":subQ0})])],"isStart":false});}
            var Q16;
            {var subQ0=sQuery(id+"F0.wireOp",EDGE,"E0");Q16=makeQuery(id+"F1.opExtrude","CAP_EDGE",EDGE,{"disambiguationData":[OSD([subQ0]),TDD([makeQuery(id+"F0.imprint","IMPRINT",EDGE,{"disambiguationData":[TD([[makeQuery(id+"F0.imprint","INTERSECT",VERTEX,{"derivedFrom":[subQ0,sQuery(id+"F0.wireOp",EDGE,"E28.MirrorCS")]}),1.0]])],"derivedFrom":subQ0})])],"isStart":false});}
            var Q17;
            {var subQ0=sQuery(id+"F0.wireOp",EDGE,"E0");Q17=makeQuery(id+"F1.opExtrude","CAP_EDGE",EDGE,{"disambiguationData":[OSD([subQ0]),TDD([makeQuery(id+"F0.imprint","IMPRINT",EDGE,{"disambiguationData":[TD([[makeQuery(id+"F0.imprint","INTERSECT",VERTEX,{"derivedFrom":[subQ0,sQuery(id+"F0.wireOp",EDGE,"E26.MirrorCS")]}),1.0]])],"derivedFrom":subQ0})])],"isStart":false});}
            var Q18;
            {var subQ0=sQuery(id+"F0.wireOp",EDGE,"E0");Q18=makeQuery(id+"F1.opExtrude","CAP_EDGE",EDGE,{"disambiguationData":[OSD([subQ0]),TDD([makeQuery(id+"F0.imprint","IMPRINT",EDGE,{"disambiguationData":[TD([[makeQuery(id+"F0.imprint","INTERSECT",VERTEX,{"derivedFrom":[subQ0,sQuery(id+"F0.wireOp",EDGE,"E24.MirrorCS")]}),1.0]])],"derivedFrom":subQ0})])],"isStart":false});}
            var Q19;
            {var subQ0=sQuery(id+"F0.wireOp",EDGE,"E0");Q19=makeQuery(id+"F1.opExtrude","CAP_EDGE",EDGE,{"disambiguationData":[OSD([subQ0]),TDD([makeQuery(id+"F0.imprint","IMPRINT",EDGE,{"disambiguationData":[TD([[makeQuery(id+"F0.imprint","INTERSECT",VERTEX,{"derivedFrom":[subQ0,sQuery(id+"F0.wireOp",EDGE,"E20.MirrorCS")]}),1.0]])],"derivedFrom":subQ0})])],"isStart":false});}
            var Q20;
            {var subQ0=sQuery(id+"F0.wireOp",EDGE,"E0");Q20=makeQuery(id+"F1.opExtrude","CAP_EDGE",EDGE,{"disambiguationData":[OSD([subQ0]),TDD([makeQuery(id+"F0.imprint","IMPRINT",EDGE,{"disambiguationData":[TD([[makeQuery(id+"F0.imprint","INTERSECT",VERTEX,{"derivedFrom":[subQ0,sQuery(id+"F0.wireOp",EDGE,"E19.MirrorCS")]}),-1.0]])],"derivedFrom":subQ0})])],"isStart":false});}
            var Q21;
            {var subQ0=sQuery(id+"F0.wireOp",EDGE,"E0");Q21=makeQuery(id+"F1.opExtrude","CAP_EDGE",EDGE,{"disambiguationData":[OSD([subQ0]),TDD([makeQuery(id+"F0.imprint","IMPRINT",EDGE,{"disambiguationData":[TD([[makeQuery(id+"F0.imprint","INTERSECT",VERTEX,{"derivedFrom":[subQ0,sQuery(id+"F0.wireOp",EDGE,"E22.MirrorCS")]}),-1.0]])],"derivedFrom":subQ0})])],"isStart":false});}
            var Q22;
            {var subQ0=sQuery(id+"F0.wireOp",EDGE,"E0");Q22=makeQuery(id+"F1.opExtrude","CAP_EDGE",EDGE,{"disambiguationData":[OSD([subQ0]),TDD([makeQuery(id+"F0.imprint","IMPRINT",EDGE,{"disambiguationData":[TD([[makeQuery(id+"F0.imprint","INTERSECT",VERTEX,{"derivedFrom":[subQ0,sQuery(id+"F0.wireOp",EDGE,"E63.MirrorCS")]}),1.0]])],"derivedFrom":subQ0})])],"isStart":false});}
            var Q23;
            {var subQ0=sQuery(id+"F0.wireOp",EDGE,"E0");Q23=makeQuery(id+"F1.opExtrude","CAP_EDGE",EDGE,{"disambiguationData":[OSD([subQ0]),TDD([makeQuery(id+"F0.imprint","IMPRINT",EDGE,{"disambiguationData":[TD([[makeQuery(id+"F0.imprint","INTERSECT",VERTEX,{"derivedFrom":[subQ0,sQuery(id+"F0.wireOp",EDGE,"E61.MirrorCS")]}),1.0]])],"derivedFrom":subQ0})])],"isStart":false});}
            var Q24;
            {var subQ0=sQuery(id+"F0.wireOp",EDGE,"E0");Q24=makeQuery(id+"F1.opExtrude","CAP_EDGE",EDGE,{"disambiguationData":[OSD([subQ0]),TDD([makeQuery(id+"F0.imprint","IMPRINT",EDGE,{"disambiguationData":[TD([[makeQuery(id+"F0.imprint","INTERSECT",VERTEX,{"derivedFrom":[subQ0,sQuery(id+"F0.wireOp",EDGE,"E59.MirrorCS")]}),1.0]])],"derivedFrom":subQ0})])],"isStart":false});}
            var Q25;
            {var subQ0=sQuery(id+"F0.wireOp",EDGE,"E0");Q25=makeQuery(id+"F1.opExtrude","CAP_EDGE",EDGE,{"disambiguationData":[OSD([subQ0]),TDD([makeQuery(id+"F0.imprint","IMPRINT",EDGE,{"disambiguationData":[TD([[makeQuery(id+"F0.imprint","INTERSECT",VERTEX,{"derivedFrom":[subQ0,sQuery(id+"F0.wireOp",EDGE,"E57.MirrorCS")]}),1.0]])],"derivedFrom":subQ0})])],"isStart":false});}
            var Q26;
            {var subQ0=sQuery(id+"F0.wireOp",EDGE,"E0");Q26=makeQuery(id+"F1.opExtrude","CAP_EDGE",EDGE,{"disambiguationData":[OSD([subQ0]),TDD([makeQuery(id+"F0.imprint","IMPRINT",EDGE,{"disambiguationData":[TD([[makeQuery(id+"F0.imprint","INTERSECT",VERTEX,{"derivedFrom":[subQ0,sQuery(id+"F0.wireOp",EDGE,"E54.MirrorCS")]}),1.0]])],"derivedFrom":subQ0})])],"isStart":false});}
            var Q27;
            {var subQ0=sQuery(id+"F0.wireOp",EDGE,"E0");Q27=makeQuery(id+"F1.opExtrude","CAP_EDGE",EDGE,{"disambiguationData":[OSD([subQ0]),TDD([makeQuery(id+"F0.imprint","IMPRINT",EDGE,{"disambiguationData":[TD([[makeQuery(id+"F0.imprint","INTERSECT",VERTEX,{"derivedFrom":[subQ0,sQuery(id+"F0.wireOp",EDGE,"E53.MirrorCS")]}),1.0]])],"derivedFrom":subQ0})])],"isStart":false});}
            var Q28;
            {var subQ0=sQuery(id+"F0.wireOp",EDGE,"E0");Q28=makeQuery(id+"F1.opExtrude","CAP_EDGE",EDGE,{"disambiguationData":[OSD([subQ0]),TDD([makeQuery(id+"F0.imprint","IMPRINT",EDGE,{"disambiguationData":[TD([[makeQuery(id+"F0.imprint","INTERSECT",VERTEX,{"derivedFrom":[subQ0,sQuery(id+"F0.wireOp",EDGE,"E51.MirrorCS")]}),1.0]])],"derivedFrom":subQ0})])],"isStart":false});}
            var Q29;
            {var subQ0=sQuery(id+"F0.wireOp",EDGE,"E0");Q29=makeQuery(id+"F1.opExtrude","CAP_EDGE",EDGE,{"disambiguationData":[OSD([subQ0]),TDD([makeQuery(id+"F0.imprint","IMPRINT",EDGE,{"disambiguationData":[TD([[makeQuery(id+"F0.imprint","INTERSECT",VERTEX,{"derivedFrom":[subQ0,sQuery(id+"F0.wireOp",EDGE,"E49.MirrorCS")]}),1.0]])],"derivedFrom":subQ0})])],"isStart":false});}
            var Q30;
            {var subQ0=sQuery(id+"F0.wireOp",EDGE,"E0");Q30=makeQuery(id+"F1.opExtrude","CAP_EDGE",EDGE,{"disambiguationData":[OSD([subQ0]),TDD([makeQuery(id+"F0.imprint","IMPRINT",EDGE,{"disambiguationData":[TD([[makeQuery(id+"F0.imprint","INTERSECT",VERTEX,{"derivedFrom":[subQ0,sQuery(id+"F0.wireOp",EDGE,"E47.MirrorCS")]}),1.0]])],"derivedFrom":subQ0})])],"isStart":false});}
            var Q31;
            {var subQ0=sQuery(id+"F0.wireOp",EDGE,"E0");Q31=makeQuery(id+"F1.opExtrude","CAP_EDGE",EDGE,{"disambiguationData":[OSD([subQ0]),TDD([makeQuery(id+"F0.imprint","IMPRINT",EDGE,{"disambiguationData":[TD([[makeQuery(id+"F0.imprint","INTERSECT",VERTEX,{"derivedFrom":[subQ0,sQuery(id+"F0.wireOp",EDGE,"E45.MirrorCS")]}),1.0]])],"derivedFrom":subQ0})])],"isStart":false});}
            fillet(context, id + "F5", {"entities" : qUnion([Q0, Q1, Q2, Q3, Q4, Q5, Q6, Q7, Q8, Q9, Q10, Q11, Q12, Q13, Q14, Q15, Q16, Q17, Q18, Q19, Q20, Q21, Q22, Q23, Q24, Q25, Q26, Q27, Q28, Q29, Q30, Q31]), "radius" : 1.27 * mm, "tangentPropagation" : true, "allowEdgeOverflow" : false});
        }
    });
